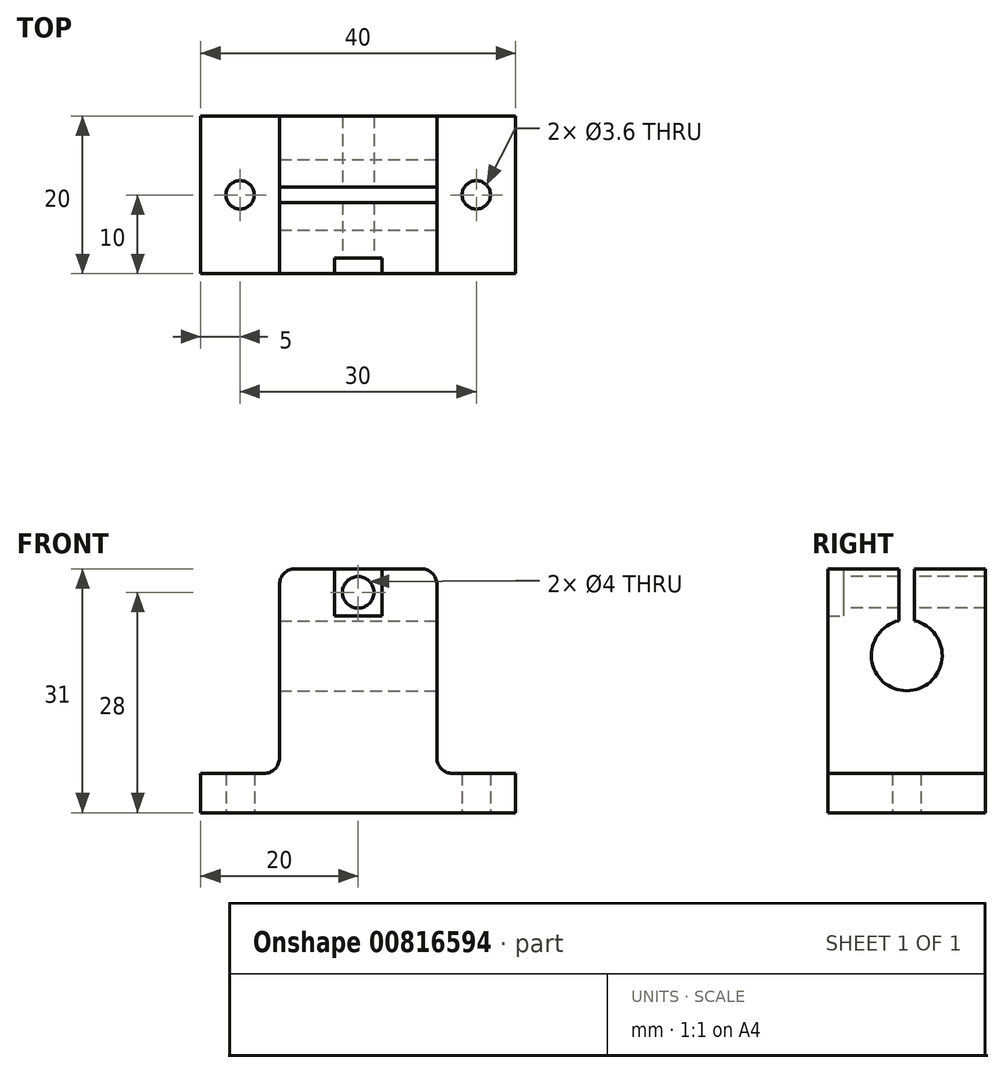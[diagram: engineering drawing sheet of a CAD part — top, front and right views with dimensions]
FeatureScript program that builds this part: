
annotation { "Feature Type Name" : "Feature", "Feature Type Description" : "" }
export const myFeature = defineFeature(function(context is Context, id is Id, definition is map)
    precondition{}
    {
        {
            var Q0;
            Q0=qCreatedBy(makeId("Front.planeOp"),FACE);
            var sketch = newSketch(context, id + "F0", { "sketchPlane" : qUnion([Q0])});
            skLineSegment(sketch, "E0", {"start": v(-10, 31) * mm, "end": v(10, 31) * mm});
            skLineSegment(sketch, "E1", {"start": v(10, 31) * mm, "end": v(10, 5) * mm});
            skLineSegment(sketch, "E2", {"start": v(10, 5) * mm, "end": v(20, 5) * mm});
            skLineSegment(sketch, "E3", {"start": v(20, 5) * mm, "end": v(20, 0) * mm});
            skLineSegment(sketch, "E4", {"start": v(20, 0) * mm, "end": v(-20, 0) * mm});
            skLineSegment(sketch, "E5", {"start": v(-20, 0) * mm, "end": v(-20, 5) * mm});
            skLineSegment(sketch, "E6", {"start": v(-20, 5) * mm, "end": v(-10, 5) * mm});
            skLineSegment(sketch, "E7", {"start": v(-10, 5) * mm, "end": v(-10, 31) * mm});
            skLineSegment(sketch, "E8", {"start": v(0, 31) * mm, "end": v(0, 0) * mm, "construction": true});
            skSolve(sketch);
        }
        {
            var Q0;
            {var subQ6=sQuery(id+"F0.wireOp",EDGE,"E1");Q0=makeQuery(id+"F0.imprint","IMPRINT",FACE,{"disambiguationData":[TD([[makeQuery(id+"F0.imprint","IMPRINT",EDGE,{"derivedFrom":subQ6}),-1.0]])]});}
            extrude(context, id + "F1", {"entities" : qUnion([Q0]), "depth" : 20 * mm, "offsetDistance" : 25 * mm});
        }
        {
            var Q0;
            Q0=makeQuery(id+"F1.opExtrude","SWEPT_FACE",FACE,{"disambiguationData":[OSD([sQuery(id+"F0.wireOp",EDGE,"E4")])]});
            var sketch = newSketch(context, id + "F2", { "sketchPlane" : qUnion([Q0])});
            skLineSegment(sketch, "E9", {"start": v(-20, 10) * mm, "end": v(20, 10) * mm, "construction": true});
            skCircle(sketch, "E10", {"center": v(-15, 10) * mm, "radius": 1.8 * mm});
            skCircle(sketch, "E11", {"center": v(15, 10) * mm, "radius": 1.8 * mm});
            skSolve(sketch);
        }
        {
            var Q0;
            Q0=makeQuery(id+"F2.imprint","IMPRINT",FACE,{"disambiguationData":[TD([[makeQuery(id+"F2.imprint","IMPRINT",EDGE,{"derivedFrom":sQuery(id+"F2.wireOp",EDGE,"E10")}),1.0]])]});
            var Q1;
            Q1=makeQuery(id+"F2.imprint","IMPRINT",FACE,{"disambiguationData":[TD([[makeQuery(id+"F2.imprint","IMPRINT",EDGE,{"derivedFrom":sQuery(id+"F2.wireOp",EDGE,"E11")}),1.0]])]});
            extrude(context, id + "F3", {"entities" : qUnion([Q0, Q1]), "operationType" : NewBodyOperationType.REMOVE, "oppositeDirection" : true, "depth" : 25 * mm, "offsetDistance" : 25 * mm});
        }
        {
            var Q0;
            Q0=makeQuery(id+"F1.opExtrude","SWEPT_FACE",FACE,{"disambiguationData":[OSD([sQuery(id+"F0.wireOp",EDGE,"E1")])]});
            var sketch = newSketch(context, id + "F4", { "sketchPlane" : qUnion([Q0])});
            skLineSegment(sketch, "E12", {"start": v(-10, 31) * mm, "end": v(-10, 5) * mm, "construction": true});
            skCircle(sketch, "E13", {"center": v(-10, 20) * mm, "radius": 4.5 * mm});
            skLineSegment(sketch, "E14", {"start": v(-11, 31) * mm, "end": v(-11, 20) * mm});
            skLineSegment(sketch, "E15", {"start": v(-11, 20) * mm, "end": v(-10, 20) * mm});
            skLineSegment(sketch, "E16.MirrorCS", {"start": v(-9, 31) * mm, "end": v(-9, 20) * mm});
            skLineSegment(sketch, "E17.MirrorCS", {"start": v(-9, 20) * mm, "end": v(-10, 20) * mm});
            skSolve(sketch);
        }
        {
            var Q0;
            {var subQ0=sQuery(id+"F4.wireOp",EDGE,"E15");Q0=makeQuery(id+"F4.imprint","IMPRINT",FACE,{"disambiguationData":[TD([[makeQuery(id+"F4.imprint","IMPRINT",EDGE,{"derivedFrom":subQ0}),-1.0]])]});}
            var Q1;
            {var subQ0=sQuery(id+"F4.wireOp",EDGE,"E14");var subQ1=sQuery(id+"F4.wireOp",EDGE,"E13");var subQ2=makeQuery(id+"F4.imprint","INTERSECT",VERTEX,{"derivedFrom":[subQ1,subQ0]});Q1=makeQuery(id+"F4.imprint","IMPRINT",FACE,{"disambiguationData":[TD([[makeQuery(id+"F4.imprint","IMPRINT",EDGE,{"disambiguationData":[TD([[subQ2,1.0]])],"derivedFrom":subQ1}),-1.0]])]});}
            var Q2;
            {var subQ4=sQuery(id+"F4.wireOp",EDGE,"E15");Q2=makeQuery(id+"F4.imprint","IMPRINT",FACE,{"disambiguationData":[TD([[makeQuery(id+"F4.imprint","IMPRINT",EDGE,{"derivedFrom":subQ4}),1.0]])]});}
            extrude(context, id + "F5", {"entities" : qUnion([Q0, Q1, Q2]), "operationType" : NewBodyOperationType.REMOVE, "oppositeDirection" : true, "depth" : 25 * mm, "offsetDistance" : 25 * mm});
        }
        {
            var Q0;
            {var subQ2=sQuery(id+"F0.wireOp",EDGE,"E0");Q0=makeQuery(id+"F5.boolean.opBoolean","SPLIT",FACE,{"disambiguationData":[TD([makeQuery(id+"F5.opExtrude","SWEPT_FACE",FACE,{"disambiguationData":[OSD([sQuery(id+"F4.wireOp",EDGE,"E14")])]})])],"derivedFrom":makeQuery(id+"F1.opExtrude","SWEPT_FACE",FACE,{"disambiguationData":[OSD([subQ2])]})});}
            var sketch = newSketch(context, id + "F6", { "sketchPlane" : qUnion([Q0])});
            skLineSegment(sketch, "E18", {"start": v(0, -20) * mm, "end": v(0, -11) * mm, "construction": true});
            skLineSegment(sketch, "E19", {"start": v(-3, -20) * mm, "end": v(-3, -18) * mm});
            skLineSegment(sketch, "E20", {"start": v(-3, -18) * mm, "end": v(0, -18) * mm});
            skLineSegment(sketch, "E21.MirrorCS", {"start": v(3, -18) * mm, "end": v(0, -18) * mm});
            skLineSegment(sketch, "E22.MirrorCS", {"start": v(3, -20) * mm, "end": v(3, -18) * mm});
            skSolve(sketch);
        }
        {
            var Q0;
            {var subQ1=sQuery(id+"F6.wireOp",EDGE,"E19");Q0=makeQuery(id+"F6.imprint","IMPRINT",FACE,{"disambiguationData":[TD([[makeQuery(id+"F6.imprint","IMPRINT",EDGE,{"derivedFrom":subQ1}),-1.0]])]});}
            extrude(context, id + "F7", {"entities" : qUnion([Q0]), "operationType" : NewBodyOperationType.REMOVE, "oppositeDirection" : true, "depth" : 6 * mm, "offsetDistance" : 25 * mm});
        }
        {
            var Q0;
            Q0=makeQuery(id+"F7.boolean.opBoolean","COPY",FACE,{"derivedFrom":makeQuery(id+"F7.opExtrude","SWEPT_FACE",FACE,{"disambiguationData":[OSD([sQuery(id+"F6.wireOp",EDGE,"E20"),sQuery(id+"F6.wireOp",EDGE,"E21.MirrorCS")])]})});
            var sketch = newSketch(context, id + "F8", { "sketchPlane" : qUnion([Q0])});
            skCircle(sketch, "E23", {"center": v(0, 28) * mm, "radius": 2 * mm});
            skPoint(sketch, "E23.centerSnap0", {"position": v(0, 31) * mm});
            skSolve(sketch);
        }
        {
            var Q0;
            Q0=makeQuery(id+"F8.imprint","IMPRINT",FACE,{"disambiguationData":[TD([[makeQuery(id+"F8.imprint","IMPRINT",EDGE,{"derivedFrom":sQuery(id+"F8.wireOp",EDGE,"E23")}),1.0]])]});
            extrude(context, id + "F9", {"entities" : qUnion([Q0]), "operationType" : NewBodyOperationType.REMOVE, "oppositeDirection" : true, "depth" : 25 * mm, "offsetDistance" : 25 * mm});
        }
        {
            var Q0;
            {var subQ0=sQuery(id+"F0.wireOp",EDGE,"E0");var subQ1=sQuery(id+"F0.wireOp",EDGE,"E1");Q0=makeQuery(id+"F5.boolean.opBoolean","SPLIT",EDGE,{"disambiguationData":[TD([makeQuery(id+"F5.opExtrude","SWEPT_FACE",FACE,{"disambiguationData":[OSD([sQuery(id+"F4.wireOp",EDGE,"E14")])]})])],"derivedFrom":makeQuery(id+"F1.opExtrude","SWEPT_EDGE",EDGE,{"disambiguationData":[OSD([subQ0,subQ1])]})});}
            var Q1;
            {var subQ0=sQuery(id+"F0.wireOp",EDGE,"E0");var subQ1=sQuery(id+"F0.wireOp",EDGE,"E1");Q1=makeQuery(id+"F5.boolean.opBoolean","SPLIT",EDGE,{"disambiguationData":[TD([makeQuery(id+"F5.opExtrude","SWEPT_FACE",FACE,{"disambiguationData":[OSD([sQuery(id+"F4.wireOp",EDGE,"E16.MirrorCS")])]})])],"derivedFrom":makeQuery(id+"F1.opExtrude","SWEPT_EDGE",EDGE,{"disambiguationData":[OSD([subQ0,subQ1])]})});}
            var Q2;
            {var subQ0=sQuery(id+"F0.wireOp",EDGE,"E0");var subQ1=sQuery(id+"F0.wireOp",EDGE,"E7");Q2=makeQuery(id+"F5.boolean.opBoolean","SPLIT",EDGE,{"disambiguationData":[TD([makeQuery(id+"F5.opExtrude","SWEPT_FACE",FACE,{"disambiguationData":[OSD([sQuery(id+"F4.wireOp",EDGE,"E16.MirrorCS")])]})])],"derivedFrom":makeQuery(id+"F1.opExtrude","SWEPT_EDGE",EDGE,{"disambiguationData":[OSD([subQ0,subQ1])]})});}
            var Q3;
            {var subQ0=sQuery(id+"F0.wireOp",EDGE,"E0");var subQ1=sQuery(id+"F0.wireOp",EDGE,"E7");Q3=makeQuery(id+"F5.boolean.opBoolean","SPLIT",EDGE,{"disambiguationData":[TD([makeQuery(id+"F5.opExtrude","SWEPT_FACE",FACE,{"disambiguationData":[OSD([sQuery(id+"F4.wireOp",EDGE,"E14")])]})])],"derivedFrom":makeQuery(id+"F1.opExtrude","SWEPT_EDGE",EDGE,{"disambiguationData":[OSD([subQ0,subQ1])]})});}
            var Q4;
            Q4=makeQuery(id+"F1.opExtrude","SWEPT_EDGE",EDGE,{"disambiguationData":[OSD([sQuery(id+"F0.wireOp",EDGE,"E1"),sQuery(id+"F0.wireOp",EDGE,"E2")])]});
            var Q5;
            Q5=makeQuery(id+"F1.opExtrude","SWEPT_EDGE",EDGE,{"disambiguationData":[OSD([sQuery(id+"F0.wireOp",EDGE,"E6"),sQuery(id+"F0.wireOp",EDGE,"E7")])]});
            fillet(context, id + "F10", {"entities" : qUnion([Q0, Q1, Q2, Q3, Q4, Q5]), "radius" : 2 * mm, "tangentPropagation" : true, "allowEdgeOverflow" : false});
        }
    });
